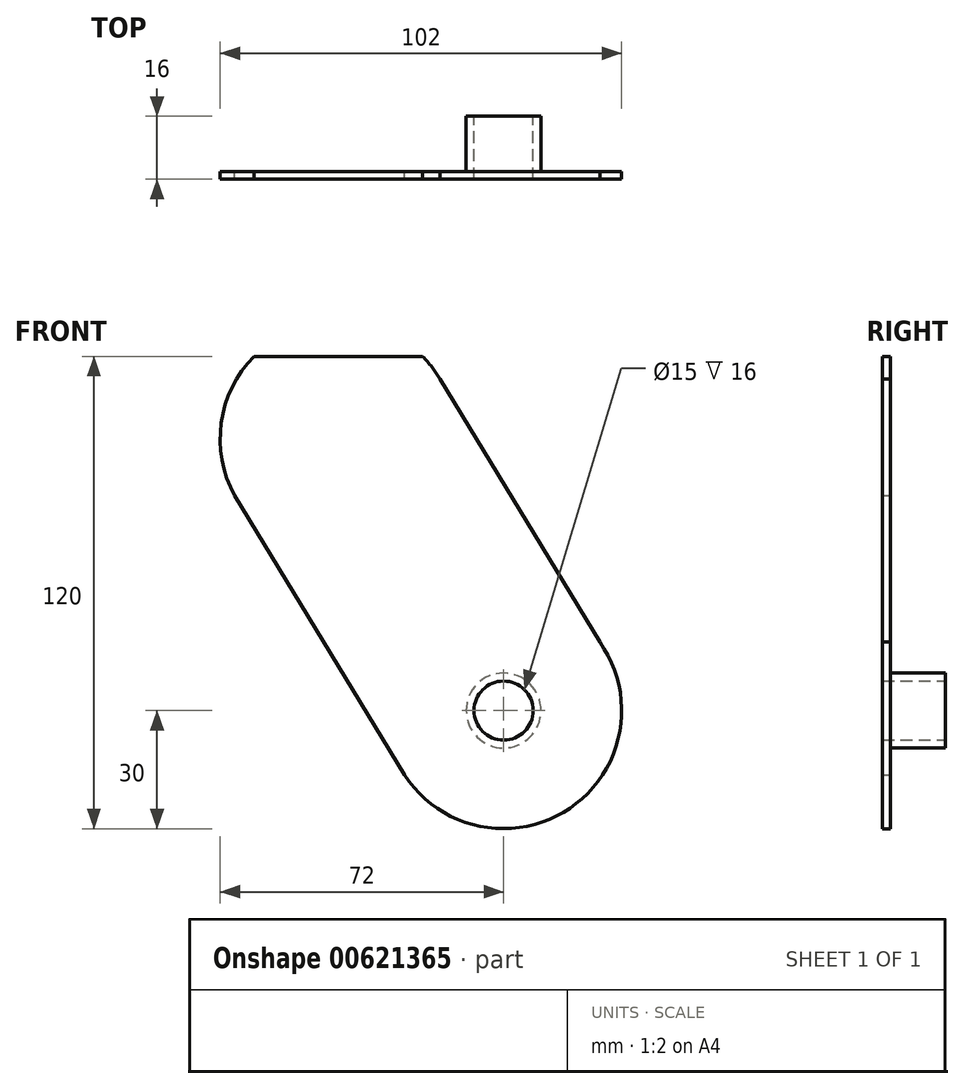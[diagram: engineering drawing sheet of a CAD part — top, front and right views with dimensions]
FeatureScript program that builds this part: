
annotation { "Feature Type Name" : "Feature", "Feature Type Description" : "" }
export const myFeature = defineFeature(function(context is Context, id is Id, definition is map)
    precondition{}
    {
        {
            var Q0;
            Q0=qCreatedBy(makeId("Front.planeOp"),FACE);
            var sketch = newSketch(context, id + "F0", { "sketchPlane" : qUnion([Q0])});
            skCircle(sketch, "E0", {"center": v(0, 0) * mm, "radius": 7.5 * mm});
            skArc(sketch, "E1", {"start": v(-25.16, -16.35) * mm, "mid": v(16.87, -24.8) * mm, "end": v(24.44, 17.4) * mm});
            skLineSegment(sketch, "E2", {"start": v(-42, 79.1) * mm, "end": v(-42, -6.08) * mm, "construction": true});
            skArc(sketch, "E3", {"start": v(-16.18, 84.27) * mm, "mid": v(-18.2, 87.27) * mm, "end": v(-20.58, 90) * mm});
            skLineSegment(sketch, "E4", {"start": v(-16.18, 84.27) * mm, "end": v(24.44, 17.4) * mm});
            skLineSegment(sketch, "E5", {"start": v(-25.16, -16.35) * mm, "end": v(-68.32, 54.6) * mm});
            skLineSegment(sketch, "E6", {"start": v(-77.1, 90) * mm, "end": v(31.4, 90) * mm, "construction": true});
            skLineSegment(sketch, "E7", {"start": v(-63.42, 90) * mm, "end": v(-20.58, 90) * mm});
            skArc(sketch, "E8.trimOffspring", {"start": v(-63.42, 90) * mm, "mid": v(-71.72, 73.1) * mm, "end": v(-68.32, 54.6) * mm});
            skCircle(sketch, "E9", {"center": v(0, 0) * mm, "radius": 81 * mm, "construction": true});
            skSolve(sketch);
        }
        {
            var Q0;
            Q0 = qSketchRegion(id + "F0", true);
            extrude(context, id + "F1", {"entities" : qUnion([Q0]), "depth" : 16 * mm, "offsetDistance" : 25 * mm});
        }
        {
            var Q0;
            Q0=makeQuery(id+"F1.opExtrude","CAP_FACE",FACE,{"disambiguationData":[OSD([sQuery(id+"F0.wireOp",EDGE,"E0"),sQuery(id+"F0.wireOp",EDGE,"E1"),sQuery(id+"F0.wireOp",EDGE,"E3"),sQuery(id+"F0.wireOp",EDGE,"E4"),sQuery(id+"F0.wireOp",EDGE,"E5"),sQuery(id+"F0.wireOp",EDGE,"E7"),sQuery(id+"F0.wireOp",EDGE,"E8.trimOffspring")])],"isStart":true});
            shell(context, id + "F2", {"entities" : qUnion([Q0]), "thickness" : 2 * mm});
        }
        {
            var Q0;
            {var subQ0=sQuery(id+"F0.wireOp",EDGE,"E8.trimOffspring");var subQ1=sQuery(id+"F0.wireOp",EDGE,"E7");var subQ2=sQuery(id+"F0.wireOp",EDGE,"E5");var subQ3=sQuery(id+"F0.wireOp",EDGE,"E4");var subQ4=sQuery(id+"F0.wireOp",EDGE,"E3");var subQ5=sQuery(id+"F0.wireOp",EDGE,"E1");var subQ6=sQuery(id+"F0.wireOp",EDGE,"E0");Q0=makeQuery(id+"F2.opShell","OFFSET_FACE",FACE,{"disambiguationData":[OSD([subQ6,subQ5,subQ4,subQ3,subQ2,subQ1,subQ0]),TDD([makeQuery(id+"F1.opExtrude","CAP_FACE",FACE,{"disambiguationData":[OSD([subQ6,subQ5,subQ4,subQ3,subQ2,subQ1,subQ0])],"isStart":true})])]});}
            extrude(context, id + "F3", {"entities" : qUnion([Q0]), "operationType" : NewBodyOperationType.REMOVE, "oppositeDirection" : true, "depth" : 14 * mm, "offsetDistance" : 25 * mm});
        }
    });
